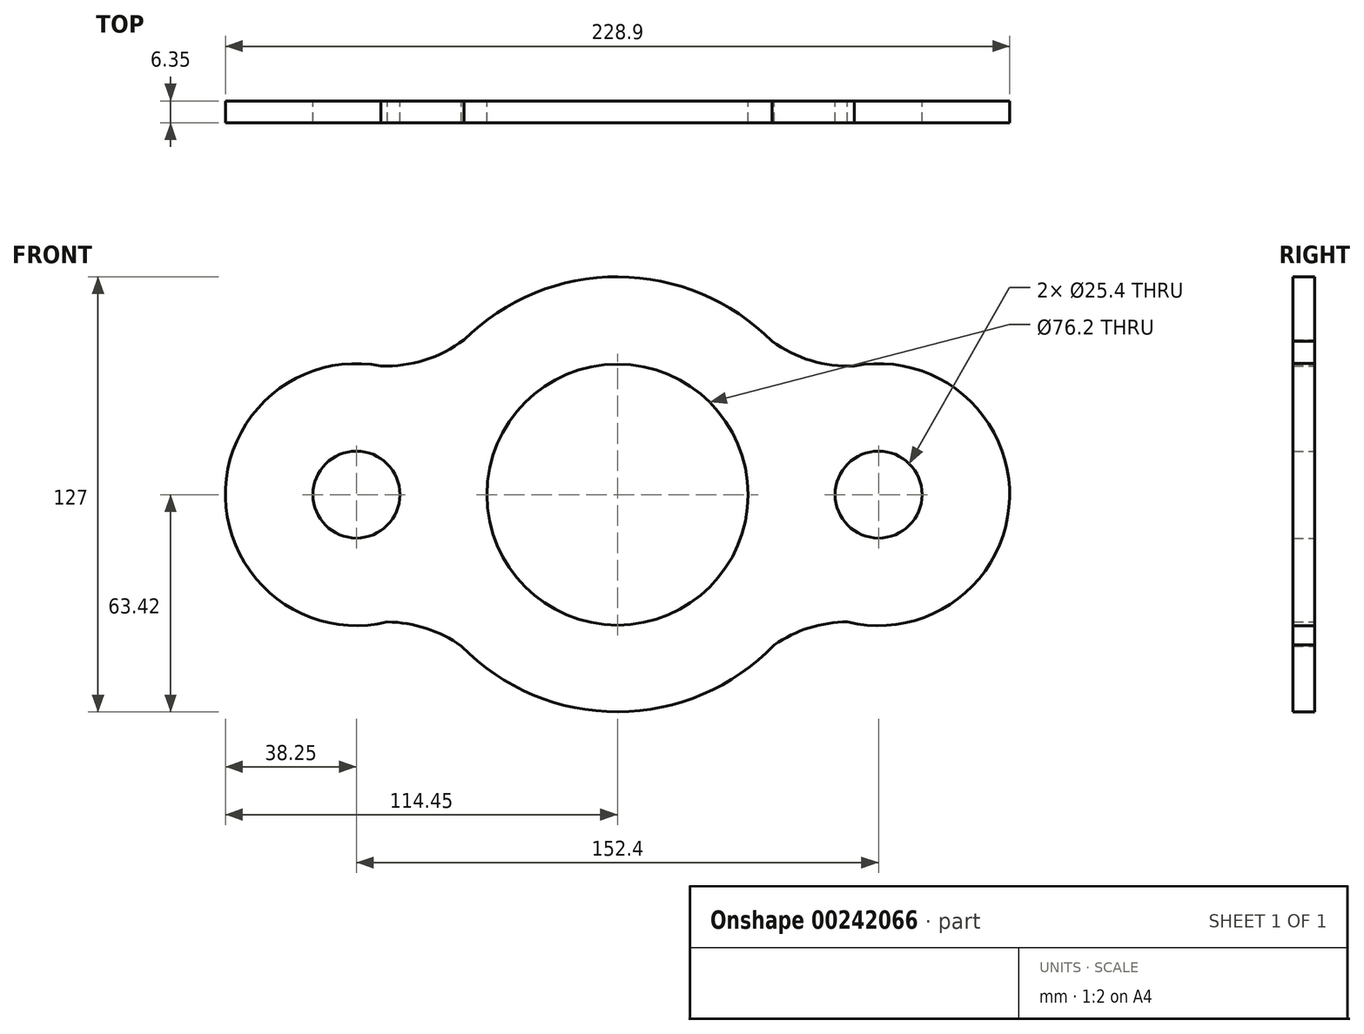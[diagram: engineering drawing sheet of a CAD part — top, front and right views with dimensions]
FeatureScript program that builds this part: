
annotation { "Feature Type Name" : "Feature", "Feature Type Description" : "" }
export const myFeature = defineFeature(function(context is Context, id is Id, definition is map)
    precondition{}
    {
        {
            var Q0;
            Q0=qCreatedBy(makeId("Front.planeOp"),FACE);
            var sketch = newSketch(context, id + "F0", { "sketchPlane" : qUnion([Q0])});
            skPoint(sketch, "E0", {"position": v(0, 0) * mm});
            skCircle(sketch, "E1", {"center": v(0, 0) * mm, "radius": 38.1 * mm});
            skCircle(sketch, "E2", {"center": v(-76.2, 0) * mm, "radius": 12.7 * mm});
            skArc(sketch, "E3", {"start": v(-69, 37.57) * mm, "mid": v(-114.44, -0.95) * mm, "end": v(-67.16, -37.16) * mm});
            skCircle(sketch, "E4.MirrorC", {"center": v(76.2, 0) * mm, "radius": 12.7 * mm});
            skArc(sketch, "E5.MirrorC", {"start": v(69.1, 37.58) * mm, "mid": v(114.44, -1) * mm, "end": v(67.15, -37.16) * mm});
            skArc(sketch, "E6", {"start": v(39.17, 50) * mm, "mid": v(55.26, 39.5) * mm, "end": v(74.44, 38.2) * mm});
            skArc(sketch, "E7.MirrorC", {"start": v(-39.9, 49.55) * mm, "mid": v(-55.92, 39.4) * mm, "end": v(-74.84, 38.22) * mm});
            skArc(sketch, "E8.MirrorC", {"start": v(-39.2, -49.94) * mm, "mid": v(-56.32, -38.89) * mm, "end": v(-76.69, -38.25) * mm});
            skArc(sketch, "E9.MirrorC", {"start": v(38.56, -50.3) * mm, "mid": v(55.78, -38.96) * mm, "end": v(76.38, -38.25) * mm});
            skArc(sketch, "E10.trimOffspring", {"start": v(-45.58, -44.22) * mm, "mid": v(0.14, -63.42) * mm, "end": v(45.73, -43.89) * mm});
            skArc(sketch, "E11.trimOffspring", {"start": v(45.06, 44.74) * mm, "mid": v(0.2, 63.58) * mm, "end": v(-44.82, 45.15) * mm});
            skSolve(sketch);
        }
        {
            var Q0;
            Q0 = qSketchRegion(id + "F0", true);
            extrude(context, id + "F1", {"entities" : qUnion([Q0]), "depth" : 6.35 * mm});
        }
    });
